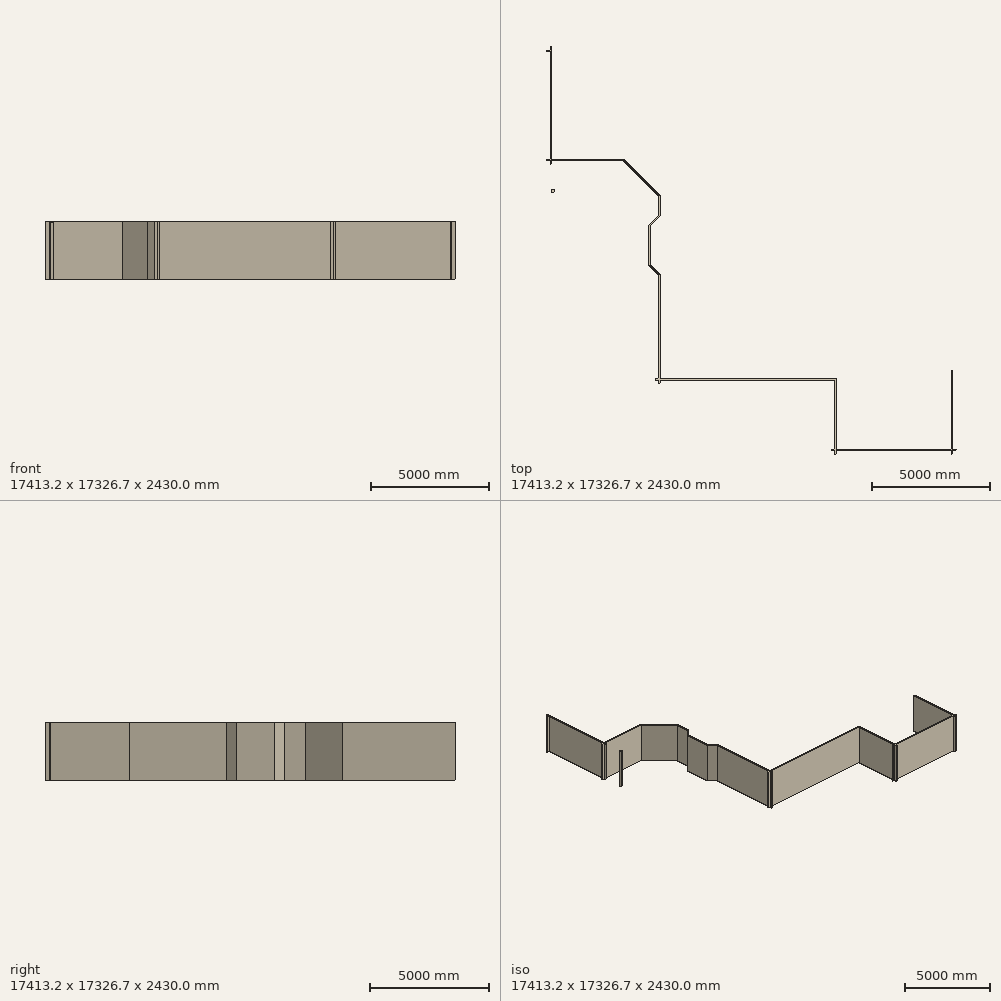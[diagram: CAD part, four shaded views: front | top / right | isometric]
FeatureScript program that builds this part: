
annotation { "Feature Type Name" : "Feature", "Feature Type Description" : "" }
export const myFeature = defineFeature(function(context is Context, id is Id, definition is map)
    precondition{}
    {
        {
            var Q0;
            Q0=qCreatedBy(makeId("Top.planeOp"),FACE);
            var sketch = newSketch(context, id + "F0", { "sketchPlane" : qUnion([Q0])});
            skLineSegment(sketch, "E0", {"start": v(0, 3398.34) * mm, "end": v(0, 70) * mm});
            skLineSegment(sketch, "E1", {"start": v(-70, 0) * mm, "end": v(-4950, 0) * mm});
            skLineSegment(sketch, "E2", {"start": v(-5020, 70) * mm, "end": v(-5020, 3000) * mm});
            skLineSegment(sketch, "E3", {"start": v(-5020, 3000) * mm, "end": v(-12430, 3000) * mm});
            skLineSegment(sketch, "E4", {"start": v(-12500, 3070) * mm, "end": v(-12500, 7455) * mm});
            skLineSegment(sketch, "E5", {"start": v(-12500, 7455) * mm, "end": v(-12924.26, 7879.26) * mm});
            skLineSegment(sketch, "E6", {"start": v(-12924.26, 7879.26) * mm, "end": v(-12924.26, 9559.26) * mm});
            skLineSegment(sketch, "E7", {"start": v(-12924.26, 9559.26) * mm, "end": v(-12500, 9983.53) * mm});
            skLineSegment(sketch, "E8", {"start": v(-12500, 9983.53) * mm, "end": v(-12500, 10813.53) * mm});
            skLineSegment(sketch, "E9", {"start": v(-12500, 10813.53) * mm, "end": v(-14013.2, 12326.74) * mm});
            skLineSegment(sketch, "E10", {"start": v(-14013.2, 12326.74) * mm, "end": v(-17043.2, 12326.74) * mm});
            skLineSegment(sketch, "E11", {"start": v(-17113.2, 12396.74) * mm, "end": v(-17113.2, 16956.74) * mm});
            skLineSegment(sketch, "E12.0", {"start": v(-17043.2, 12396.74) * mm, "end": v(-17043.2, 17026.74) * mm});
            skLineSegment(sketch, "E13.0", {"start": v(-12430, 10842.52) * mm, "end": v(-13984.21, 12396.74) * mm});
            skLineSegment(sketch, "E14.0", {"start": v(-12430, 9954.53) * mm, "end": v(-12430, 10842.52) * mm});
            skLineSegment(sketch, "E14.1", {"start": v(-12854.26, 9530.27) * mm, "end": v(-12430, 9954.53) * mm});
            skLineSegment(sketch, "E15.0", {"start": v(-12854.26, 7908.26) * mm, "end": v(-12854.26, 9530.27) * mm});
            skLineSegment(sketch, "E16.0", {"start": v(-12430, 7484) * mm, "end": v(-12854.26, 7908.26) * mm});
            skLineSegment(sketch, "E17.0", {"start": v(-12430, 3070) * mm, "end": v(-12430, 7484) * mm});
            skLineSegment(sketch, "E18.0", {"start": v(-4950, 3070) * mm, "end": v(-12430, 3070) * mm});
            skLineSegment(sketch, "E19.0", {"start": v(-4950, 70) * mm, "end": v(-4950, 3070) * mm});
            skLineSegment(sketch, "E20.0", {"start": v(-70, 70) * mm, "end": v(-4950, 70) * mm});
            skLineSegment(sketch, "E21.0", {"start": v(-70, 3398.34) * mm, "end": v(-70, 70) * mm});
            skLineSegment(sketch, "E22", {"start": v(-70, 3398.34) * mm, "end": v(0, 3398.34) * mm});
            skLineSegment(sketch, "E23", {"start": v(-13984.21, 12396.74) * mm, "end": v(-17043.2, 12396.74) * mm});
            skLineSegment(sketch, "E24", {"start": v(-17113.2, 12326.74) * mm, "end": v(-17113.2, 12176.74) * mm});
            skLineSegment(sketch, "E25", {"start": v(-17113.2, 12176.74) * mm, "end": v(-17043.2, 12176.74) * mm});
            skLineSegment(sketch, "E26", {"start": v(-17043.2, 12176.74) * mm, "end": v(-17043.2, 12326.74) * mm});
            skLineSegment(sketch, "E27", {"start": v(-17113.2, 12326.74) * mm, "end": v(-17263.2, 12326.74) * mm});
            skLineSegment(sketch, "E28", {"start": v(-17263.2, 12326.74) * mm, "end": v(-17263.2, 12396.74) * mm});
            skLineSegment(sketch, "E29", {"start": v(-17263.2, 12396.74) * mm, "end": v(-17113.2, 12396.74) * mm});
            skLineSegment(sketch, "E30", {"start": v(-12500, 3000) * mm, "end": v(-12650, 3000) * mm});
            skLineSegment(sketch, "E31", {"start": v(-12650, 3000) * mm, "end": v(-12650, 3070) * mm});
            skLineSegment(sketch, "E32", {"start": v(-12650, 3070) * mm, "end": v(-12500, 3070) * mm});
            skLineSegment(sketch, "E33", {"start": v(-12500, 3000) * mm, "end": v(-12500, 2850) * mm});
            skLineSegment(sketch, "E34", {"start": v(-12500, 2850) * mm, "end": v(-12430, 2850) * mm});
            skLineSegment(sketch, "E35", {"start": v(-12430, 2850) * mm, "end": v(-12430, 3000) * mm});
            skLineSegment(sketch, "E36", {"start": v(-5020, 0) * mm, "end": v(-5170, 0) * mm});
            skLineSegment(sketch, "E37", {"start": v(-5170, 0) * mm, "end": v(-5170, 70) * mm});
            skLineSegment(sketch, "E38", {"start": v(-5170, 70) * mm, "end": v(-5020, 70) * mm});
            skLineSegment(sketch, "E39", {"start": v(-5020, 0) * mm, "end": v(-5020, -150) * mm});
            skLineSegment(sketch, "E40", {"start": v(-5020, -150) * mm, "end": v(-4950, -150) * mm});
            skLineSegment(sketch, "E41", {"start": v(-4950, -150) * mm, "end": v(-4950, 0) * mm});
            skLineSegment(sketch, "E42", {"start": v(0, 0) * mm, "end": v(150, 0) * mm});
            skLineSegment(sketch, "E43", {"start": v(150, 0) * mm, "end": v(150, 70) * mm});
            skLineSegment(sketch, "E44", {"start": v(150, 70) * mm, "end": v(0, 70) * mm});
            skLineSegment(sketch, "E45", {"start": v(0, 0) * mm, "end": v(0, -150) * mm});
            skLineSegment(sketch, "E46", {"start": v(0, -150) * mm, "end": v(-70, -150) * mm});
            skLineSegment(sketch, "E47", {"start": v(-70, -150) * mm, "end": v(-70, 0) * mm});
            skLineSegment(sketch, "E48", {"start": v(-17043.2, 11066.74) * mm, "end": v(-17043.2, 10946.74) * mm});
            skLineSegment(sketch, "E49", {"start": v(-17043.2, 10946.74) * mm, "end": v(-16923.2, 10946.74) * mm});
            skLineSegment(sketch, "E50", {"start": v(-16923.2, 10946.74) * mm, "end": v(-16923.2, 11066.74) * mm});
            skLineSegment(sketch, "E51", {"start": v(-16923.2, 11066.74) * mm, "end": v(-17043.2, 11066.74) * mm});
            skLineSegment(sketch, "E52", {"start": v(-17113.2, 17026.74) * mm, "end": v(-17263.2, 17026.74) * mm});
            skLineSegment(sketch, "E53", {"start": v(-17263.2, 17026.74) * mm, "end": v(-17263.2, 16956.74) * mm});
            skLineSegment(sketch, "E54", {"start": v(-17263.2, 16956.74) * mm, "end": v(-17113.2, 16956.74) * mm});
            skLineSegment(sketch, "E55", {"start": v(-17113.2, 17026.74) * mm, "end": v(-17113.2, 17176.74) * mm});
            skLineSegment(sketch, "E56", {"start": v(-17113.2, 17176.74) * mm, "end": v(-17043.2, 17176.74) * mm});
            skLineSegment(sketch, "E57", {"start": v(-17043.2, 17176.74) * mm, "end": v(-17043.2, 17026.74) * mm});
            skSolve(sketch);
        }
        {
            var Q0;
            Q0=makeQuery(id+"F0.imprint","IMPRINT",FACE,{"disambiguationData":[TD([[makeQuery(id+"F0.imprint","IMPRINT",EDGE,{"derivedFrom":sQuery(id+"F0.wireOp",EDGE,"E0")}),-1.0]])]});
            extrude(context, id + "F1", {"entities" : qUnion([Q0]), "depth" : 2430 * mm, "offsetDistance" : 25 * mm});
        }
        {
            var Q0;
            Q0=qCreatedBy(makeId("Top.planeOp"),FACE);
            var sketch = newSketch(context, id + "F2", { "sketchPlane" : qUnion([Q0])});
            skLineSegment(sketch, "E58", {"start": v(-17043.2, 11096.74) * mm, "end": v(-17043.2, 10976.74) * mm});
            skLineSegment(sketch, "E59", {"start": v(-17043.2, 10976.74) * mm, "end": v(-16923.2, 10976.74) * mm});
            skLineSegment(sketch, "E60", {"start": v(-16923.2, 10976.74) * mm, "end": v(-16923.2, 11096.74) * mm});
            skLineSegment(sketch, "E61", {"start": v(-16923.2, 11096.74) * mm, "end": v(-17043.2, 11096.74) * mm});
            skSolve(sketch);
        }
        {
            var Q0;
            Q0=makeQuery(id+"F2.imprint","IMPRINT",FACE,{"disambiguationData":[TD([[makeQuery(id+"F2.imprint","IMPRINT",EDGE,{"derivedFrom":sQuery(id+"F2.wireOp",EDGE,"E58")}),1.0]])]});
            extrude(context, id + "F3", {"entities" : qUnion([Q0]), "depth" : 2400 * mm, "offsetDistance" : 25 * mm});
        }
    });
